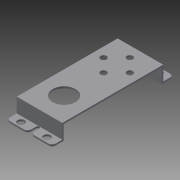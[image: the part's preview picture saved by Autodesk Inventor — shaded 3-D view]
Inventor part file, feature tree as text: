
AUTODESK INVENTOR PART (.ipt)
format: ipt  version: 2014 SP2 (Build 180246200, 246)  size: 195,072 bytes
history: native  units: in
note: dims shown in document units (in); Inventor stores cm internally (conversion verified against a paired STEP export)
features: extrude x5, sketch x4, projected_geometry x3, fillet x2
ambient origin geometry x8: Origin, YZ Plane, XZ Plane, XY Plane, X Axis, Y Axis, Z Axis, Center Point
bodies: Solid1 (feature_tree)
feature tree (14):
  sketch  "Sketch1"  dims[d0=0.0394in d1=0.0in d2=0.035in]
  extrude  "Extrusion1"  Depth=0.035in
  extrude  "Extrusion2"  Depth=0.348in TaperAngle=0.0deg
  extrude  "Extrusion3"  Depth=0.08in
  fillet  "Fillet1"  Radius=0.04in
  fillet  "Fillet2"  Radius=5.0in
  extrude  "Extrusion4"  Depth=0.3937in
  extrude  "Extrusion5"  Depth=0.3937in
  sketch  "Sketch2"  dims[d3=0.035in d4=0.348in d5=0.0in]
  projected_geometry  "Projected Loop1"
  projected_geometry  "Projected Loop2"
  projected_geometry  "Projected Loop3"
  sketch  "Sketch3"  dims[d6=0.0394in d7=0.0in d8=0.08in d9=0.04in d10=5.0in d11=0.0in]
  sketch  "Sketch4"  dims[d12=0.315in d13=0.7874in d15=1.26in d16=0.3937in d18=1.0in d20=0.315in d21=0.146in d22=1.5748in d24=360.0deg d26=5.0in d27=0.0in]
